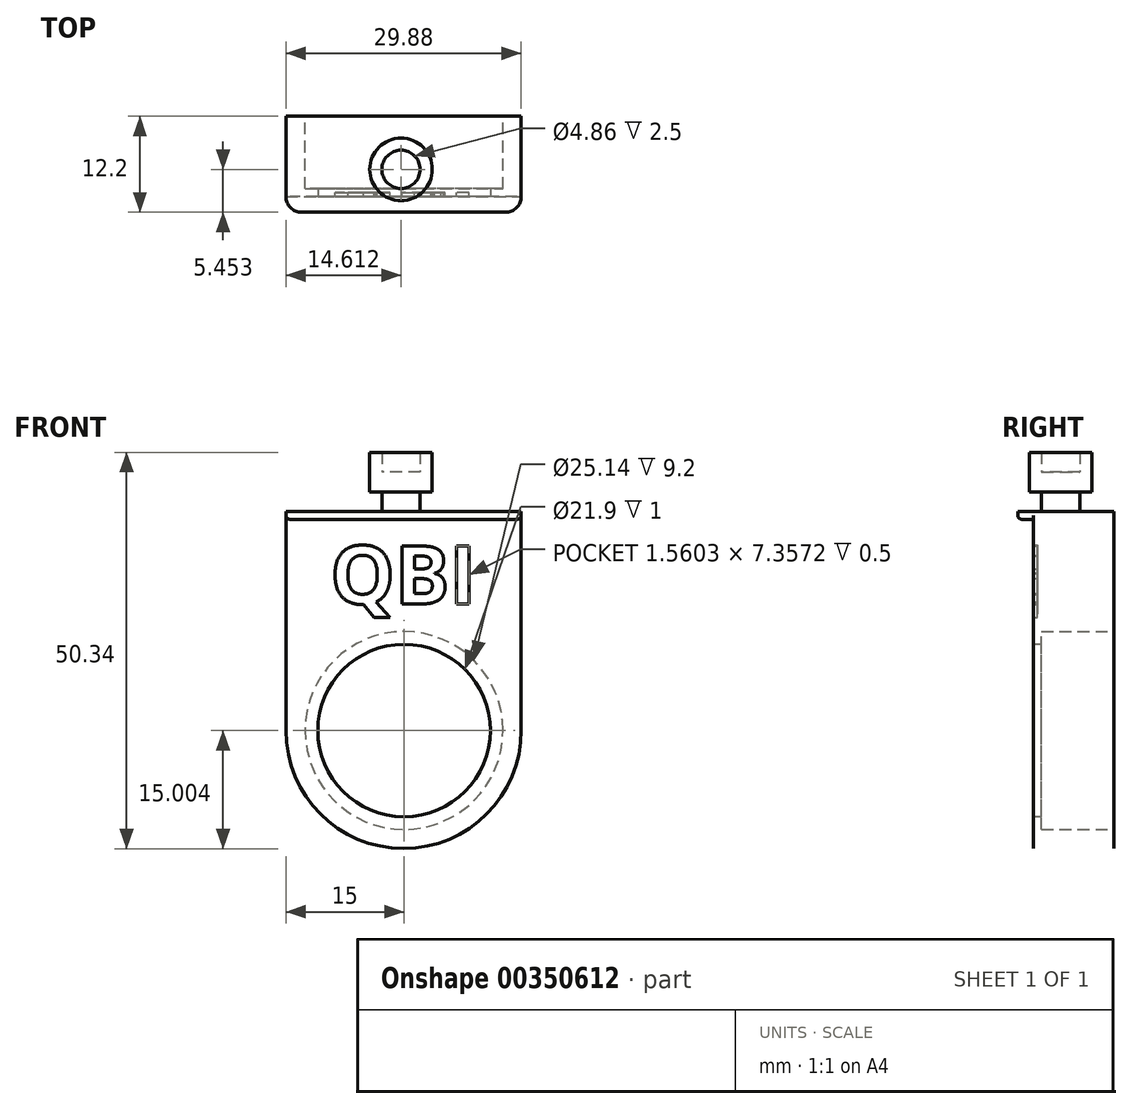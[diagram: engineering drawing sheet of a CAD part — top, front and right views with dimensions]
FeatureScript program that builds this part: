
annotation { "Feature Type Name" : "Feature", "Feature Type Description" : "" }
export const myFeature = defineFeature(function(context is Context, id is Id, definition is map)
    precondition{}
    {
        {
            var Q0;
            Q0=qCreatedBy(makeId("Front.planeOp"),FACE);
            var sketch = newSketch(context, id + "F0", { "sketchPlane" : qUnion([Q0])});
            skLineSegment(sketch, "E0.bottom", {"start": v(9.3, 9.2) * mm, "end": v(-20.58, 9.2) * mm});
            skLineSegment(sketch, "E0.top", {"start": v(-5.58, -33.64) * mm, "end": v(-5.7, -33.64) * mm});
            skLineSegment(sketch, "E0.left", {"start": v(9.3, 9.2) * mm, "end": v(9.3, -18.64) * mm});
            skLineSegment(sketch, "E0.right", {"start": v(-20.58, 9.2) * mm, "end": v(-20.58, -18.64) * mm});
            skPoint(sketch, "E1.visualSharp", {"position": v(9.3, -33.64) * mm});
            skArc(sketch, "E1.filletArc", {"start": v(-5.7, -33.64) * mm, "mid": v(4.9, -29.24) * mm, "end": v(9.3, -18.64) * mm});
            skPoint(sketch, "E2.visualSharp", {"position": v(-20.58, -33.64) * mm});
            skArc(sketch, "E2.filletArc", {"start": v(-20.58, -18.64) * mm, "mid": v(-16.19, -29.24) * mm, "end": v(-5.58, -33.64) * mm});
            skCircle(sketch, "E3", {"center": v(-5.58, -18.64) * mm, "radius": 12.57 * mm});
            skSolve(sketch);
        }
        {
            var Q0;
            Q0=makeQuery(id+"F0.imprint","IMPRINT",FACE,{"disambiguationData":[TD([[makeQuery(id+"F0.imprint","IMPRINT",EDGE,{"derivedFrom":sQuery(id+"F0.wireOp",EDGE,"E0.bottom")}),1.0]])]});
            extrude(context, id + "F1", {"entities" : qUnion([Q0]), "depth" : 10.2 * mm});
        }
        {
            var Q0;
            Q0=makeQuery(id+"F1.opExtrude","CAP_FACE",FACE,{"disambiguationData":[OSD([sQuery(id+"F0.wireOp",EDGE,"E0.bottom"),sQuery(id+"F0.wireOp",EDGE,"E0.left"),sQuery(id+"F0.wireOp",EDGE,"E0.right"),sQuery(id+"F0.wireOp",EDGE,"E1.filletArc"),sQuery(id+"F0.wireOp",EDGE,"E2.filletArc"),sQuery(id+"F0.wireOp",EDGE,"E3")])],"isStart":false});
            var sketch = newSketch(context, id + "F2", { "sketchPlane" : qUnion([Q0])});
            skCircle(sketch, "E4", {"center": v(-5.58, -18.64) * mm, "radius": 10.95 * mm});
            skSolve(sketch);
        }
        {
            var Q0;
            Q0=makeQuery(id+"F2.imprint","IMPRINT",FACE,{"disambiguationData":[TD([[makeQuery(id+"F2.imprint","IMPRINT",EDGE,{"derivedFrom":sQuery(id+"F2.wireOp",EDGE,"E4")}),-1.0]])]});
            extrude(context, id + "F3", {"entities" : qUnion([Q0]), "operationType" : NewBodyOperationType.ADD, "oppositeDirection" : true, "depth" : 1 * mm});
        }
        {
            var Q0;
            Q0=makeQuery(id+"F1.opExtrude","SWEPT_FACE",FACE,{"disambiguationData":[OSD([sQuery(id+"F0.wireOp",EDGE,"E0.bottom")])]});
            var sketch = newSketch(context, id + "F4", { "sketchPlane" : qUnion([Q0])});
            skLineSegment(sketch, "E5.bottom", {"start": v(-20.58, -10.2) * mm, "end": v(9.3, -10.2) * mm});
            skLineSegment(sketch, "E5.top", {"start": v(-18.58, -12.2) * mm, "end": v(7.3, -12.2) * mm});
            skLineSegment(sketch, "E5.left", {"start": v(-20.58, -10.2) * mm, "end": v(-20.58, -10.2) * mm});
            skLineSegment(sketch, "E5.right", {"start": v(9.3, -10.2) * mm, "end": v(9.3, -10.2) * mm});
            skPoint(sketch, "E6.visualSharp", {"position": v(-20.58, -12.2) * mm});
            skArc(sketch, "E6.filletArc", {"start": v(-20.58, -10.2) * mm, "mid": v(-20, -11.61) * mm, "end": v(-18.58, -12.2) * mm});
            skPoint(sketch, "E7.visualSharp", {"position": v(9.3, -12.2) * mm});
            skArc(sketch, "E7.filletArc", {"start": v(7.3, -12.2) * mm, "mid": v(8.71, -11.61) * mm, "end": v(9.3, -10.2) * mm});
            skSolve(sketch);
        }
        {
            var Q0;
            Q0=makeQuery(id+"F4.imprint","IMPRINT",FACE,{"disambiguationData":[TD([[makeQuery(id+"F4.imprint","IMPRINT",EDGE,{"derivedFrom":sQuery(id+"F4.wireOp",EDGE,"E5.bottom")}),1.0]])]});
            extrude(context, id + "F5", {"entities" : qUnion([Q0]), "operationType" : NewBodyOperationType.ADD, "oppositeDirection" : true, "depth" : 1 * mm});
        }
        {
            var Q0;
            Q0=makeQuery(id+"F5.opExtrude","CAP_EDGE",EDGE,{"disambiguationData":[OSD([sQuery(id+"F4.wireOp",EDGE,"E5.top")])],"isStart":false});
            var Q1;
            Q1=makeQuery(id+"F5.opExtrude","CAP_EDGE",EDGE,{"disambiguationData":[OSD([sQuery(id+"F4.wireOp",EDGE,"E6.filletArc")])],"isStart":false});
            var Q2;
            Q2=makeQuery(id+"F5.opExtrude","CAP_EDGE",EDGE,{"disambiguationData":[OSD([sQuery(id+"F4.wireOp",EDGE,"E7.filletArc")])],"isStart":false});
            fillet(context, id + "F6", {"entities" : qUnion([Q0, Q1, Q2]), "radius" : 0.5 * mm, "tangentPropagation" : true, "allowEdgeOverflow" : false});
        }
        {
            var Q0;
            {var subQ0=sQuery(id+"F0.wireOp",EDGE,"E3");Q0=makeQuery(id+"F3.boolean.opBoolean","MERGE",FACE,{"derivedFrom":[makeQuery(id+"F1.opExtrude","CAP_FACE",FACE,{"disambiguationData":[OSD([sQuery(id+"F0.wireOp",EDGE,"E0.bottom"),sQuery(id+"F0.wireOp",EDGE,"E0.left"),sQuery(id+"F0.wireOp",EDGE,"E0.right"),sQuery(id+"F0.wireOp",EDGE,"E1.filletArc"),sQuery(id+"F0.wireOp",EDGE,"E2.filletArc"),subQ0])],"isStart":false}),makeQuery(id+"F3.opExtrude","CAP_FACE",FACE,{"disambiguationData":[OSD([subQ0,sQuery(id+"F2.wireOp",EDGE,"E4")])],"isStart":true})]});}
            var sketch = newSketch(context, id + "F7", { "sketchPlane" : qUnion([Q0])});
            skText(sketch, "E8", { "text": "QBI", "fontName": "OpenSans-Bold.ttf"});
            const initialGuessF7  = {"E8": [-0.01495, -0.00254, 1, 0, 0.00742]};
            skSetInitialGuess(sketch, initialGuessF7);
            skSolve(sketch);
        }
        {
            var Q0;
            Q0 = qSketchRegion(id + "F7", true);
            extrude(context, id + "F8", {"entities" : qUnion([Q0]), "operationType" : NewBodyOperationType.REMOVE, "endBound" : BoundingType.SYMMETRIC, "depth" : 1 * mm});
        }
        {
            var Q0;
            Q0=makeQuery(id+"F5.boolean.opBoolean","MERGE",FACE,{"derivedFrom":[makeQuery(id+"F1.opExtrude","SWEPT_FACE",FACE,{"disambiguationData":[OSD([sQuery(id+"F0.wireOp",EDGE,"E0.bottom")])]}),makeQuery(id+"F5.opExtrude","CAP_FACE",FACE,{"disambiguationData":[OSD([sQuery(id+"F4.wireOp",EDGE,"E5.bottom"),sQuery(id+"F4.wireOp",EDGE,"E5.top"),sQuery(id+"F4.wireOp",EDGE,"E6.filletArc"),sQuery(id+"F4.wireOp",EDGE,"E7.filletArc")])],"isStart":true})]});
            var sketch = newSketch(context, id + "F9", { "sketchPlane" : qUnion([Q0])});
            skCircle(sketch, "E9", {"center": v(-5.97, -6.75) * mm, "radius": 2.43 * mm});
            skSolve(sketch);
        }
        {
            var Q0;
            Q0=makeQuery(id+"F9.imprint","IMPRINT",FACE,{"disambiguationData":[TD([[makeQuery(id+"F9.imprint","IMPRINT",EDGE,{"derivedFrom":sQuery(id+"F9.wireOp",EDGE,"E9")}),1.0]])]});
            var Q1;
            Q1=sQuery(id+"F9.wireOp",EDGE,"E9");
            extrude(context, id + "F10", {"entities" : qUnion([Q0]), "operationType" : NewBodyOperationType.ADD, "surfaceEntities" : qUnion([Q1]), "depth" : 5 * mm});
        }
        {
            var Q0;
            Q0=makeQuery(id+"F10.opExtrude","CAP_FACE",FACE,{"disambiguationData":[OSD([sQuery(id+"F9.wireOp",EDGE,"E9")])],"isStart":false});
            var sketch = newSketch(context, id + "F11", { "sketchPlane" : qUnion([Q0])});
            skCircle(sketch, "E10", {"center": v(-5.97, -6.75) * mm, "radius": 3.97 * mm});
            skSolve(sketch);
        }
        {
            var Q0;
            Q0=makeQuery(id+"F11.imprint","IMPRINT",FACE,{"disambiguationData":[TD([[makeQuery(id+"F11.imprint","IMPRINT",EDGE,{"derivedFrom":sQuery(id+"F11.wireOp",EDGE,"E10")}),1.0]])]});
            var Q1;
            Q1=sQuery(id+"F11.wireOp",EDGE,"E10");
            extrude(context, id + "F12", {"entities" : qUnion([Q0]), "operationType" : NewBodyOperationType.ADD, "surfaceEntities" : qUnion([Q1]), "endBound" : BoundingType.SYMMETRIC, "depth" : 5 * mm});
        }
    });
